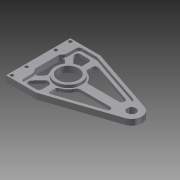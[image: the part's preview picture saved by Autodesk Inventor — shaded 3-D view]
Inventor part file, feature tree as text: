
AUTODESK INVENTOR PART (.ipt)
format: ipt  version: 2012 (Build 160160000, 160)  size: 259,072 bytes
history: native  units: in
note: dims shown in document units (in); Inventor stores cm internally (conversion verified against a paired STEP export)
features: extrude x3, fillet x3, sketch x2, hole x1
ambient origin geometry x8: Origin, YZ Plane, XZ Plane, XY Plane, X Axis, Y Axis, Z Axis, Center Point
bodies: Solid1 (feature_tree)
feature tree (9):
  sketch  "Sketch1"  dims[d0=2.75in d1=4.0in]
  extrude  "Extrusion1"  Depth=4.0in
  extrude  "Extrusion2"  Depth=0.1279in
  fillet  "Fillet1"  Radius=0.375in
  hole  "Hole1"  [1 undecoded]
  sketch  "Sketch2"  dims[d2=1.375in d6=0.1279in d7=0.375in d8=1.289in d9=0.875in d10=0.125in d11=0.0in d12=0.625in d13=0.1875in d14=0.1875in d15=0.25in d16=0.25in d17=0.125in d18=0.125in d19=0.125in d20=0.125in d21=0.125in d22=0.125in d24=0.125in d25=0.125in d26=0.25in d27=0.375in d28=0.25in d29=0.125in d30=0.0in d31=0.125in d32=0.125in d33=0.125in d35=0.125in d36=0.125in d38=0.144in d39=0.75in d40=0.25in d41=0.25in d42=0.5635in d43=1.0in d44=0.8108in d45=0.5in d46=0.125in d47=0.125in d48=0.125in d49=0.125in d51=0.125in d53=0.875in d54=0.0625in d58=0.125in d59=0.0in d62=0.75in d63=0.75in d69=0.125in d70=0.1279in d71=0.4375in d72=1.125in d73=0.125in d74=0.25in]
  extrude  "Extrusion4"  Depth=0.875in
  fillet  "Fillet6"  Radius=0.125in
  fillet  "Fillet7"  Radius=0.625in
note: 1 required parameter value undecoded (feature->parameter linkage not recoverable at this tier; creation-order binding heuristic only, values carry confidence <= 0.55)
